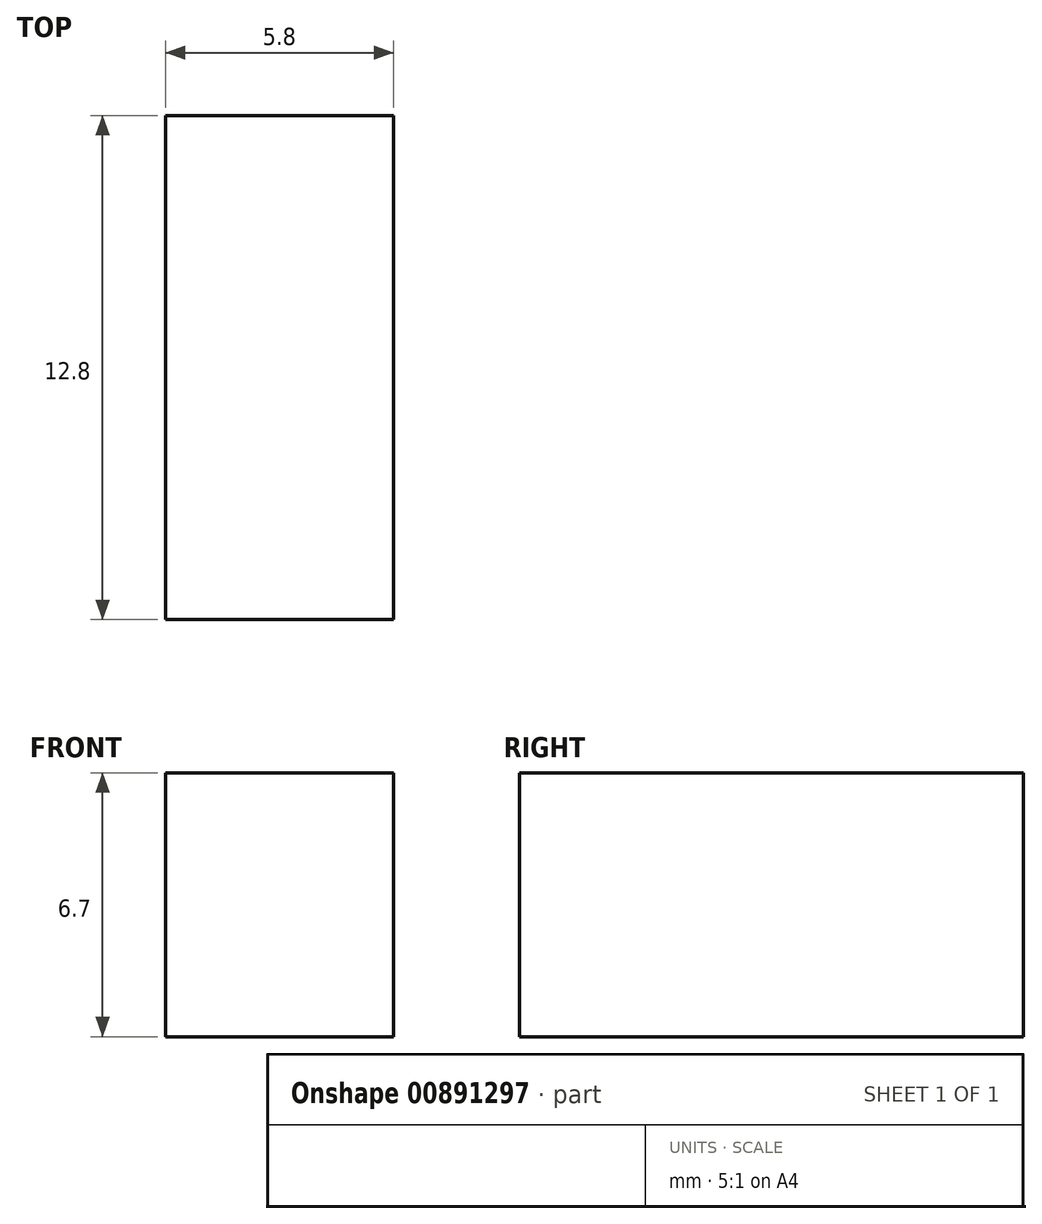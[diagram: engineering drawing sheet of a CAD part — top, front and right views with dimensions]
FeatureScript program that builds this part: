
annotation { "Feature Type Name" : "Feature", "Feature Type Description" : "" }
export const myFeature = defineFeature(function(context is Context, id is Id, definition is map)
    precondition{}
    {
        {
            var Q0;
            Q0=qCreatedBy(makeId("Top.planeOp"),FACE);
            var sketch = newSketch(context, id + "F0", { "sketchPlane" : qUnion([Q0])});
            skLineSegment(sketch, "E0.bottom", {"start": v(2.9, -6.4) * mm, "end": v(-2.9, -6.4) * mm});
            skLineSegment(sketch, "E0.top", {"start": v(2.9, 6.4) * mm, "end": v(-2.9, 6.4) * mm});
            skLineSegment(sketch, "E0.left", {"start": v(2.9, -6.4) * mm, "end": v(2.9, 6.4) * mm});
            skLineSegment(sketch, "E0.right", {"start": v(-2.9, -6.4) * mm, "end": v(-2.9, 6.4) * mm});
            skPoint(sketch, "E0.middle", {"position": v(0, 0) * mm});
            skSolve(sketch);
        }
        {
            var Q0;
            Q0 = qSketchRegion(id + "F0", true);
            extrude(context, id + "F1", {"entities" : qUnion([Q0]), "depth" : 6.7 * mm, "offsetDistance" : 25 * mm});
        }
    });
